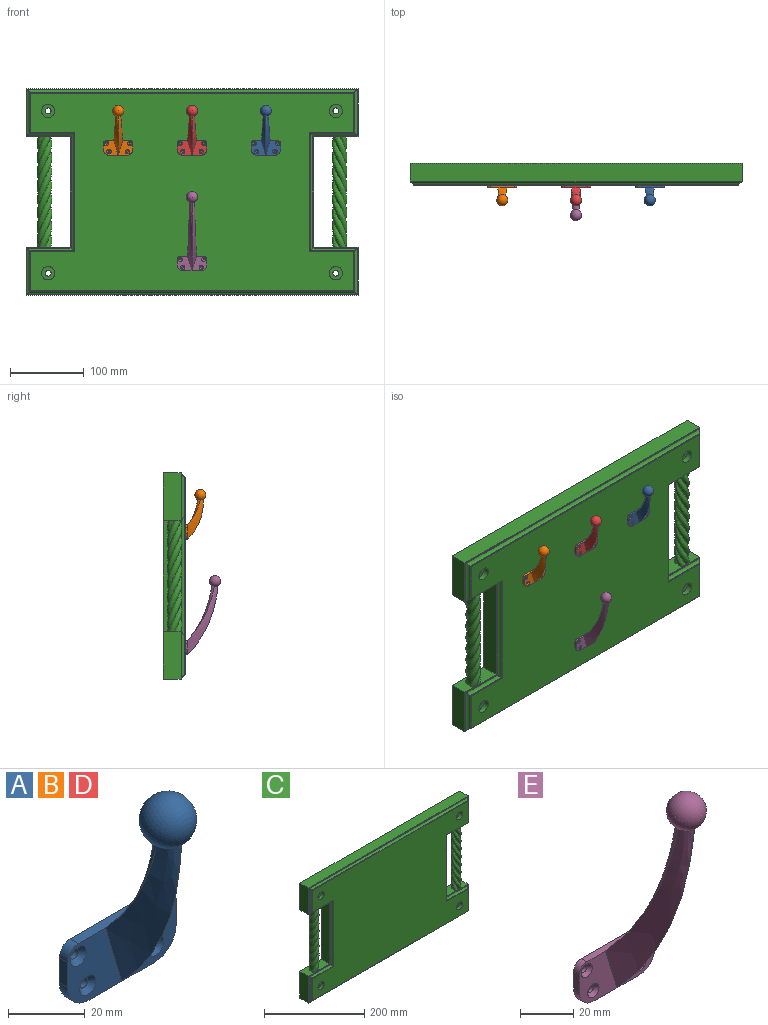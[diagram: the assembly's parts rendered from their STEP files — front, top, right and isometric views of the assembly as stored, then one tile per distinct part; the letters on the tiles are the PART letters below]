
ASSEMBLY  parts=5 mates=2
PART A: 23 faces, bbox 40x27.5x67.5 mm
  f0: plane 20x20mm, normal (0,-1,0), area 266.3mm2, adj f1,f2,f3,f7,f12,f16,f17,f19
  f1: plane 8x3mm, normal (1,0,0), area 24mm2, adj f0,f2,f12,f13
  f2: cylinder r=4mm len=4mm, axis (0,-1,0), area 18.8mm2, adj f0,f1,f3,f13
  f3: plane 32x3mm, normal (0,0,1), area 96mm2, adj f0,f2,f4,f13,f14,f20
  f4: cylinder r=4mm len=4mm, axis (0,-1,0), area 18.8mm2, adj f3,f5,f13,f14
  f5: plane 8x3mm, normal (-1,0,0), area 24mm2, adj f4,f6,f13,f14
  f6: cylinder r=8mm len=8mm, axis (0,-1,0), area 37.7mm2, adj f5,f7,f13,f14
  f7: plane 24x3mm, normal (0,0,-1), area 72mm2, adj f0,f6,f12,f13,f14
  f8: cylinder r=1.5mm len=3mm, axis (0,-1,0), area 14.1mm2, adj f13,f18
  f9: cylinder r=1.5mm len=3mm, axis (0,-1,0), area 14.1mm2, adj f13,f17
  f10: cylinder r=1.5mm len=3mm, axis (0,-1,0), area 14.1mm2, adj f13,f15
  f11: cylinder r=1.5mm len=3mm, axis (0,-1,0), area 14.1mm2, adj f13,f16
  f12: cylinder r=8mm len=8mm, axis (0,-1,0), area 37.7mm2, adj f0,f1,f7,f13
  f13: plane 40x20mm, normal (0,1,0), area 737.4mm2, adj f1,f2,f3,f4,f5,f6,f7,f8
  f14: plane 20x20mm, normal (0,-1,0), area 266.3mm2, adj f3,f4,f5,f6,f7,f15,f18,f21
  f15: cone r=1.5mm half-angle=45deg, axis (0,-1,0), area 30mm2, adj f10,f14
  f16: cone r=1.5mm half-angle=45deg, axis (0,-1,0), area 30mm2, adj f0,f11
  f17: cone r=1.5mm half-angle=45deg, axis (0,-1,0), area 30mm2, adj f0,f9
  f18: cone r=1.5mm half-angle=45deg, axis (0,-1,0), area 30mm2, adj f8,f14
  f19: bspline ~55.68x21.38mm, area 513.9mm2, adj f0,f20,f21,f22
  f20: bspline ~40x17mm, area 391.4mm2, adj f3,f19,f21,f22
  f21: bspline ~55.68x21.38mm, area 513.9mm2, adj f14,f19,f20,f22
  f22: sphere r=7.5mm, area 661.5mm2, adj f19,f20,f21
PART B: same geometry as A
PART C: 72 faces, bbox 450x32.4x280 mm
  f0: cylinder r=4mm len=22mm, axis (0,-1,0), area 552.9mm2, adj f16,f62
  f1: cylinder r=4mm len=22mm, axis (0,-1,0), area 552.9mm2, adj f16,f60
  f2: cylinder r=4mm len=22mm, axis (0,-1,0), area 552.9mm2, adj f16,f58
  f3: cylinder r=4mm len=22mm, axis (0,-1,0), area 552.9mm2, adj f16,f56
  f4: plane 65x24mm, normal (1,0,0), area 1560mm2, adj f5,f15,f16,f54
  f5: plane 450x24mm, normal (0,0,1), area 10800mm2, adj f4,f7,f16,f54
  f6: plane 65x24mm, normal (1,0,0), area 1560mm2, adj f12,f13,f16,f54
  f7: plane 65x24mm, normal (-1,0,0), area 1560mm2, adj f5,f8,f16,f54
  f8: plane 60x24mm, normal (0,0,-1), area 1182.9mm2, adj f7,f9,f16,f54,f64,f65,f66,f67
  f9: plane 150x24mm, normal (-1,0,0), area 3600mm2, adj f8,f10,f16,f54
  f10: plane 60x24mm, normal (0,0,1), area 1182.9mm2, adj f9,f11,f16,f54,f64,f65,f66,f67
  f11: plane 65x24mm, normal (-1,0,0), area 1560mm2, adj f10,f12,f16,f54
  f12: plane 450x24mm, normal (0,0,-1), area 10800mm2, adj f6,f11,f16,f54
  f13: plane 60x24mm, normal (0,0,1), area 1182.9mm2, adj f6,f14,f16,f54,f68,f69,f70,f71
  f14: plane 150x24mm, normal (1,0,0), area 3600mm2, adj f13,f15,f16,f54
  f15: plane 60x24mm, normal (0,0,-1), area 1182.9mm2, adj f4,f14,f16,f54,f68,f69,f70,f71
  f16: plane 450x280mm, normal (0,1,0), area 107798.9mm2, adj f0,f1,f2,f3,f4,f5,f6,f7
  f17: plane 438x1mm, normal (0,0,-1), area 438mm2, adj f20,f23,f51,f55
  f18: cylinder r=5mm len=448mm, axis (-1,0,0), area 2589.2mm2, adj f19,f21,f24,f51
  f19: plane 448x1.1mm, normal (0,0,-1), area 493.3mm2, adj f18,f22,f25,f54
  f20: plane 53x1mm, normal (-1,0,0), area 53mm2, adj f17,f28,f51,f55
  f21: cylinder r=5mm len=63mm, axis (0,0,1), area 340.6mm2, adj f18,f22,f27,f51
  f22: plane 63x1.1mm, normal (-1,0,0), area 69.4mm2, adj f19,f21,f26,f54
  f23: plane 53x1mm, normal (1,0,0), area 53mm2, adj f17,f29,f51,f55
  f24: cylinder r=5mm len=63mm, axis (0,0,-1), area 340.6mm2, adj f18,f25,f30,f51
  f25: plane 63x1.1mm, normal (1,0,0), area 69.4mm2, adj f19,f24,f31,f54
  f26: plane 60x1.1mm, normal (0,0,1), area 66.1mm2, adj f22,f27,f32,f54
  f27: cylinder r=5mm len=63.9mm, axis (1,0,0), area 350.4mm2, adj f21,f26,f33,f51
  f28: plane 60x1mm, normal (0,0,1), area 60mm2, adj f20,f34,f51,f55
  f29: plane 60x1mm, normal (0,0,1), area 60mm2, adj f23,f37,f51,f55
  f30: cylinder r=5mm len=63.9mm, axis (1,0,0), area 350.4mm2, adj f24,f31,f36,f51
  f31: plane 60x1.1mm, normal (0,0,1), area 66.1mm2, adj f25,f30,f35,f54
  f32: plane 152x1.1mm, normal (-1,0,0), area 167.4mm2, adj f26,f33,f40,f54
  f33: cylinder r=5mm len=159.8mm, axis (0,0,1), area 915.1mm2, adj f27,f32,f39,f51
  f34: plane 162x1mm, normal (-1,0,0), area 162mm2, adj f28,f38,f51,f55
  f35: plane 152x1.1mm, normal (1,0,0), area 167.4mm2, adj f31,f36,f41,f54
  f36: cylinder r=5mm len=159.8mm, axis (0,0,-1), area 915.1mm2, adj f30,f35,f42,f51
  f37: plane 162x1mm, normal (1,0,0), area 162mm2, adj f29,f43,f51,f55
  f38: plane 60x1mm, normal (0,0,-1), area 60mm2, adj f34,f44,f51,f55
  f39: cylinder r=5mm len=63.9mm, axis (-1,0,0), area 350.4mm2, adj f33,f40,f45,f51
  f40: plane 60x1.1mm, normal (0,0,-1), area 66.1mm2, adj f32,f39,f46,f54
  f41: plane 60x1.1mm, normal (0,0,-1), area 66.1mm2, adj f35,f42,f49,f54
  f42: cylinder r=5mm len=63.9mm, axis (-1,0,0), area 350.4mm2, adj f36,f41,f48,f51
  f43: plane 60x1mm, normal (0,0,-1), area 60mm2, adj f37,f47,f51,f55
  f44: plane 53x1mm, normal (-1,0,0), area 53mm2, adj f38,f50,f51,f55
  f45: cylinder r=5mm len=63mm, axis (0,0,1), area 340.6mm2, adj f39,f46,f51,f52
  f46: plane 63x1.1mm, normal (-1,0,0), area 69.4mm2, adj f40,f45,f53,f54
  f47: plane 53x1mm, normal (1,0,0), area 53mm2, adj f43,f50,f51,f55
  f48: cylinder r=5mm len=63mm, axis (0,0,-1), area 340.6mm2, adj f42,f49,f51,f52
  f49: plane 63x1.1mm, normal (1,0,0), area 69.4mm2, adj f41,f48,f53,f54
  f50: plane 438x1mm, normal (0,0,1), area 438mm2, adj f44,f47,f51,f55
  f51: plane 440.2x270.2mm, normal (0,-1,0), area 1823.7mm2, adj f17,f18,f20,f21,f23,f24,f27,f28
  f52: cylinder r=5mm len=448mm, axis (1,0,0), area 2589.2mm2, adj f45,f48,f51,f53
  f53: plane 448x1.1mm, normal (0,0,1), area 493.3mm2, adj f46,f49,f52,f54
  f54: plane 450x280mm, normal (0,-1,0), area 1696mm2, adj f4,f5,f6,f7,f8,f9,f10,f11
  f55: plane 438x268mm, normal (0,-1,0), area 96926.1mm2, adj f17,f20,f23,f28,f29,f34,f37,f38
  f56: plane 18x18mm, normal (0,-1,0), area 204.2mm2, adj f3,f57
  f57: cylinder r=9mm len=18mm, axis (0,-1,0), area 452.4mm2, adj f55,f56
  f58: plane 18x18mm, normal (0,-1,0), area 204.2mm2, adj f2,f59
  f59: cylinder r=9mm len=18mm, axis (0,-1,0), area 452.4mm2, adj f55,f58
  f60: plane 18x18mm, normal (0,-1,0), area 204.2mm2, adj f1,f61
  f61: cylinder r=9mm len=18mm, axis (0,-1,0), area 452.4mm2, adj f55,f60
  f62: plane 18x18mm, normal (0,-1,0), area 204.2mm2, adj f0,f63
  f63: cylinder r=9mm len=18mm, axis (0,-1,0), area 452.4mm2, adj f55,f62
  f64: bspline ~150x32.43mm, area 2457.6mm2, adj f8,f10,f65,f67
  f65: bspline ~150x32.43mm, area 2457.6mm2, adj f8,f10,f64,f66
  f66: bspline ~150x32.43mm, area 2457.6mm2, adj f8,f10,f65,f67
  f67: bspline ~150x32.43mm, area 2457.6mm2, adj f8,f10,f64,f66
  f68: bspline ~150x32.43mm, area 2457.6mm2, adj f13,f15,f69,f71
  f69: bspline ~150x32.43mm, area 2457.6mm2, adj f13,f15,f68,f70
  f70: bspline ~150x32.43mm, area 2457.6mm2, adj f13,f15,f69,f71
  f71: bspline ~150x32.43mm, area 2457.6mm2, adj f13,f15,f68,f70
PART D: same geometry as A
PART E: 23 faces, bbox 40x47.5x107.5 mm
  f0: plane 20x20mm, normal (0,-1,0), area 266.3mm2, adj f1,f3,f4,f8,f10,f16,f17,f19
  f1: plane 32x3mm, normal (0,0,1), area 96mm2, adj f0,f5,f6,f7,f8,f20
  f2: plane 8x3mm, normal (-1,0,0), area 24mm2, adj f5,f6,f7,f9
  f3: plane 24x3mm, normal (0,0,-1), area 72mm2, adj f0,f5,f6,f9,f10
  f4: plane 8x3mm, normal (1,0,0), area 24mm2, adj f0,f5,f8,f10
  f5: plane 40x20mm, normal (0,1,0), area 737.4mm2, adj f1,f2,f3,f4,f7,f8,f9,f10
  f6: plane 20x20mm, normal (0,-1,0), area 266.3mm2, adj f1,f2,f3,f7,f9,f15,f18,f21
  f7: cylinder r=4mm len=4mm, axis (0,1,0), area 18.8mm2, adj f1,f2,f5,f6
  f8: cylinder r=4mm len=4mm, axis (0,-1,0), area 18.8mm2, adj f0,f1,f4,f5
  f9: cylinder r=8mm len=8mm, axis (0,-1,0), area 37.7mm2, adj f2,f3,f5,f6
  f10: cylinder r=8mm len=8mm, axis (0,1,0), area 37.7mm2, adj f0,f3,f4,f5
  f11: cylinder r=1.5mm len=3mm, axis (0,-1,0), area 14.1mm2, adj f5,f15
  f12: cylinder r=1.5mm len=3mm, axis (0,-1,0), area 14.1mm2, adj f5,f16
  f13: cylinder r=1.5mm len=3mm, axis (0,-1,0), area 14.1mm2, adj f5,f17
  f14: cylinder r=1.5mm len=3mm, axis (0,-1,0), area 14.1mm2, adj f5,f18
  f15: cone r=1.5mm half-angle=45deg, axis (0,-1,0), area 30mm2, adj f6,f11
  f16: cone r=1.5mm half-angle=45deg, axis (0,-1,0), area 30mm2, adj f0,f12
  f17: cone r=1.5mm half-angle=45deg, axis (0,-1,0), area 30mm2, adj f0,f13
  f18: cone r=1.5mm half-angle=45deg, axis (0,-1,0), area 30mm2, adj f6,f14
  f19: bspline ~94.6x40.73mm, area 982.3mm2, adj f0,f20,f21,f22
  f20: bspline ~80x37mm, area 870.2mm2, adj f1,f19,f21,f22
  f21: bspline ~94.6x40.73mm, area 982.3mm2, adj f6,f19,f20,f22
  f22: sphere r=7.5mm, area 663.3mm2, adj f19,f20,f21
PLACE A t=(91.3,-13.56,73.99)mm
PLACE B t=(-108.7,-13.56,73.99)mm
PLACE C t=(-8.7,19.44,14.19)mm
PLACE D t=(-8.7,-13.56,73.99)mm
PLACE E t=(-8.7,-13.56,-82.81)mm
MATE planar E.f5 <-> C.f55  axis (0,1,0) through (-8.7,-10.56,-92.81)mm
MATE planar A.f13 <-> C.f55  axis (0,1,0) through (91.3,-10.56,74.19)mm
